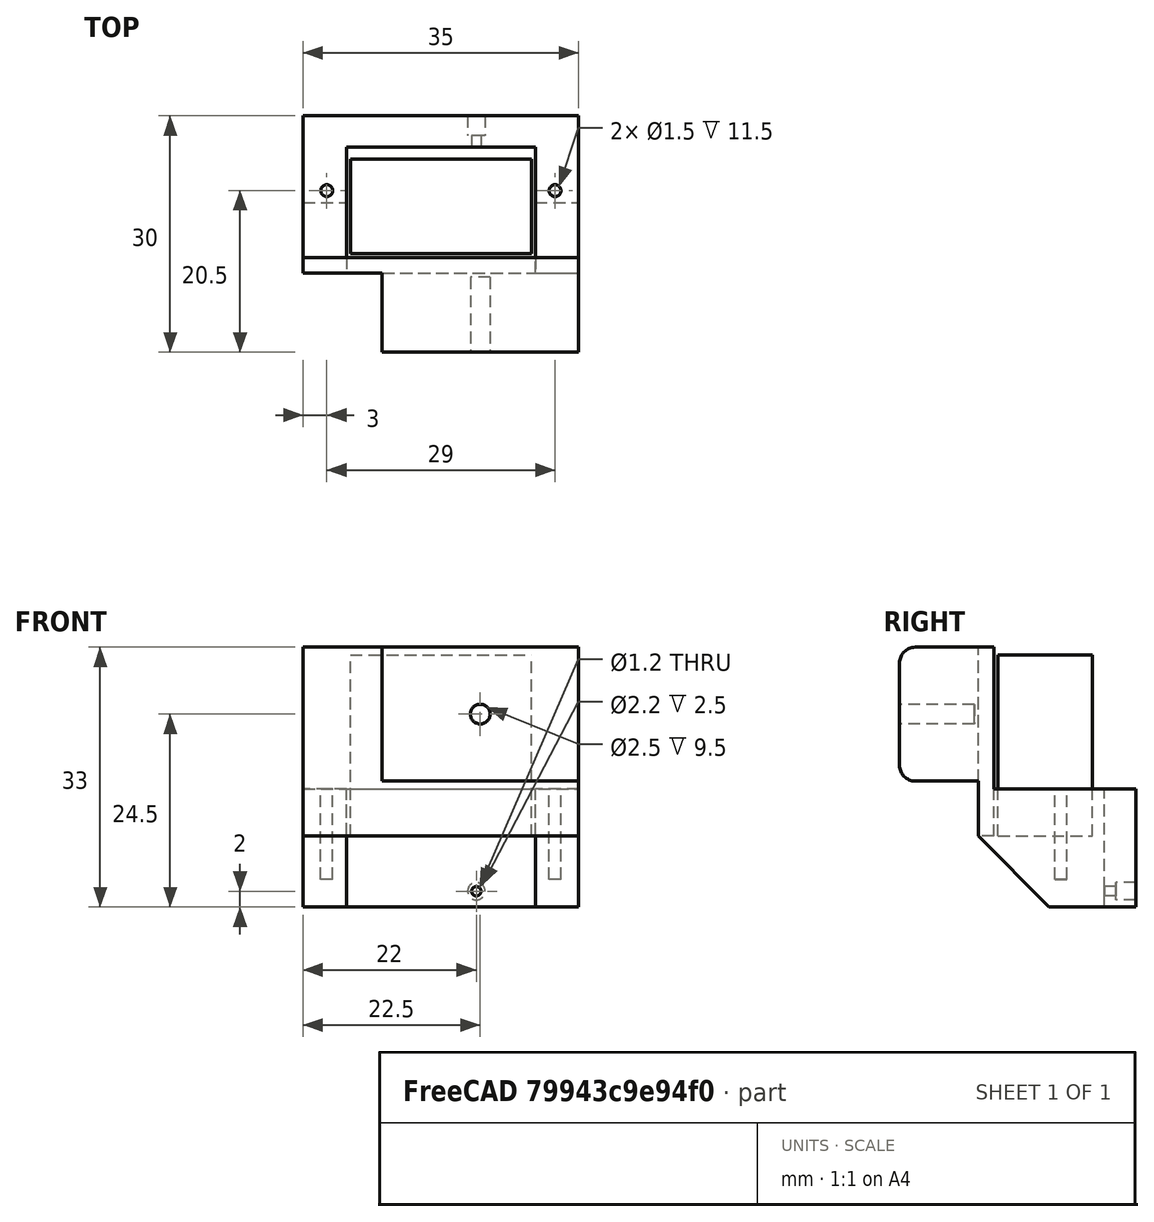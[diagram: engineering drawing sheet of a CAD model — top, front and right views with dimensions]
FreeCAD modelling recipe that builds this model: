
FCSTD DOCUMENT  (FreeCAD 0.15R3918 (Git))
Label: diff-lock-servo-mount
License: CC-BY 3.0
LicenseURL: http://creativecommons.org/licenses/by/3.0/
objects: Part::Box×6, Part::Cylinder×5, Part::MultiFuse×4, Part::Cut×3, Part::Fillet×1, Part::Chamfer×1
note: 20 computed .brp shape members not serialized (recipe doc carries the construction recipe); baked Part::Feature solids carry a one-line shape summary decoded from their .brp

FEATURE [Part::Box] Box001
  Height = 17
  Length = 25
  Placement = pos=(0,0,1.5) rot=(0,0,1;0rad)
  Width = 10
FEATURE [Part::Fillet] Fillet001
  Base = -> Box001
  Edges = 2 edges r=2: [Edge9,Edge10]
  Placement = pos=(-1,0.5,-1) rot=(0,0,1;0rad)
FEATURE [Part::Box] Box003  label="servo"
  Height = 23
  Length = 23
  Placement = pos=(-5,13,-6.5) rot=(0,0,1;0rad)
  Width = 12
FEATURE [Part::Box] Box004
  Height = 15
  Length = 5.5
  Placement = pos=(-11,10.5,-15.5) rot=(0,0,1;0rad)
  Width = 20
FEATURE [Part::Box] Box005
  Height = 24
  Length = 35
  Placement = pos=(-11,10.5,-6.5) rot=(0,0,1;0rad)
  Width = 2
FEATURE [Part::Cylinder] Cylinder
  Angle = 360
  Height = 4
  Placement = pos=(0,30.5,0) rot=(1,0,0;1.5708rad)
  Radius = 1.1
FEATURE [Part::Cylinder] Cylinder001
  Angle = 360
  Height = 7
  Placement = pos=(0,30.5,0) rot=(1,0,0;1.5708rad)
  Radius = 0.6
FEATURE [Part::MultiFuse] Fusion001
  Placement = pos=(11,1.5,-13.5) rot=(0,0,1;0rad)
  Shapes = -> [Cylinder,Cylinder001]
FEATURE [Part::Box] Box
  Height = 15
  Length = 5.5
  Placement = pos=(18.5,10.5,-15.5) rot=(0,0,1;0rad)
  Width = 20
FEATURE [Part::Box] Box006
  Height = 15
  Length = 35
  Placement = pos=(-11,26.5,-15.5) rot=(0,0,1;0rad)
  Width = 4
FEATURE [Part::MultiFuse] Fusion
  Shapes = -> [Box004,Box,Box006,Box005]
FEATURE [Part::Cut] Cut
  Base = -> Fusion
  Tool = -> Fusion001
FEATURE [Part::Chamfer] Chamfer
  Base = -> Cut
  Edges = 2 edges r=9: [Edge22,Edge23]
FEATURE [Part::MultiFuse] Fusion002
  Shapes = -> [Fillet001,Chamfer]
FEATURE [Part::Cylinder] Cylinder002
  Angle = 360
  Height = 12
  Radius = 0.75
FEATURE [Part::Cylinder] Cylinder003
  Angle = 360
  Height = 12
  Placement = pos=(29,0,0) rot=(0,0,1;0rad)
  Radius = 0.75
FEATURE [Part::MultiFuse] Fusion003
  Placement = pos=(-8,21,-12) rot=(0,0,1;0rad)
  Shapes = -> [Cylinder002,Cylinder003]
FEATURE [Part::Cut] Cut001
  Base = -> Fusion002
  Tool = -> Fusion003
FEATURE [Part::Cylinder] Cylinder004
  Angle = 360
  Height = 10
  Placement = pos=(11.5,10,9) rot=(1,0,0;1.5708rad)
  Radius = 1.25
FEATURE [Part::Cut] Cut002
  Base = -> Cut001
  Tool = -> Cylinder004
